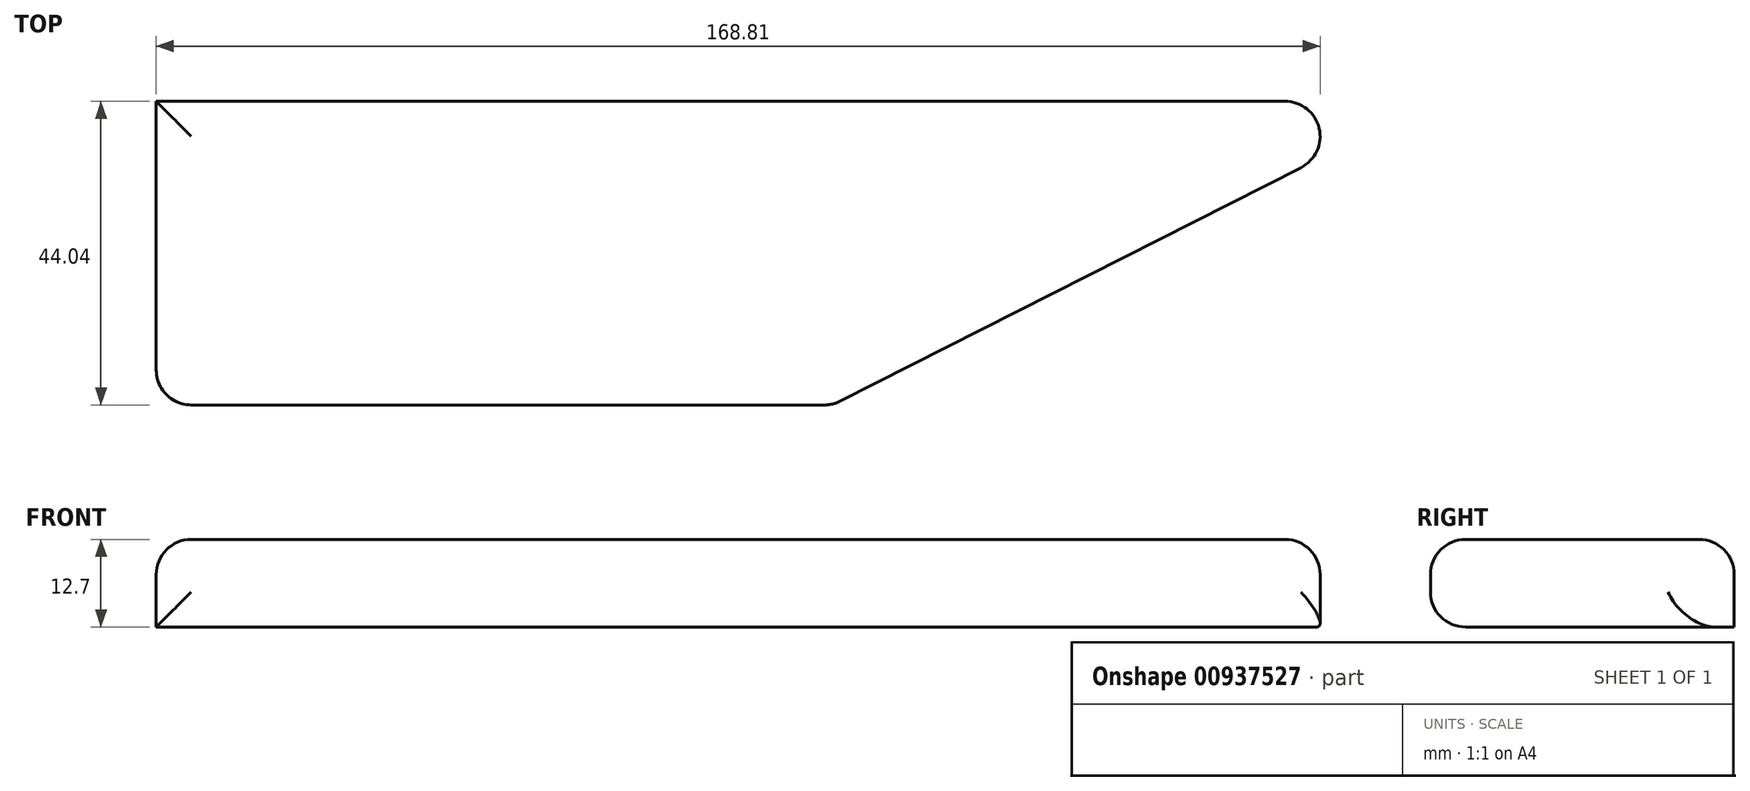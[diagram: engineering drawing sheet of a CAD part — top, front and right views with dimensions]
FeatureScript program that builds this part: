
annotation { "Feature Type Name" : "Feature", "Feature Type Description" : "" }
export const myFeature = defineFeature(function(context is Context, id is Id, definition is map)
    precondition{}
    {
        {
            var Q0;
            Q0=qCreatedBy(makeId("Top.planeOp"),FACE);
            var sketch = newSketch(context, id + "F0", { "sketchPlane" : qUnion([Q0])});
            skLineSegment(sketch, "E0", {"start": v(-44.9, 21.4) * mm, "end": v(-44.9, -24.6) * mm});
            skLineSegment(sketch, "E1", {"start": v(-44.9, -24.6) * mm, "end": v(53.22, -24.6) * mm});
            skLineSegment(sketch, "E2", {"start": v(53.22, -24.6) * mm, "end": v(140.08, 19.45) * mm});
            skLineSegment(sketch, "E3", {"start": v(140.08, 19.45) * mm, "end": v(-44.9, 19.45) * mm});
            skSolve(sketch);
        }
        {
            var Q0;
            {var subQ0=sQuery(id+"F0.wireOp",EDGE,"E1");Q0=makeQuery(id+"F0.imprint","IMPRINT",FACE,{"disambiguationData":[TD([[makeQuery(id+"F0.imprint","IMPRINT",EDGE,{"derivedFrom":subQ0}),1.0]])]});}
            extrude(context, id + "F1", {"entities" : qUnion([Q0]), "depth" : 12.7 * mm, "offsetDistance" : 25.4 * mm});
        }
        {
            var Q0;
            Q0=makeQuery(id+"F1.opExtrude","CAP_FACE",FACE,{"disambiguationData":[OSD([sQuery(id+"F0.wireOp",EDGE,"E0"),sQuery(id+"F0.wireOp",EDGE,"E1"),sQuery(id+"F0.wireOp",EDGE,"E2"),sQuery(id+"F0.wireOp",EDGE,"E3")])],"isStart":false});
            var Q1;
            Q1=makeQuery(id+"F1.opExtrude","SWEPT_FACE",FACE,{"disambiguationData":[OSD([sQuery(id+"F0.wireOp",EDGE,"E1")])]});
            var Q2;
            Q2=makeQuery(id+"F1.opExtrude","SWEPT_FACE",FACE,{"disambiguationData":[OSD([sQuery(id+"F0.wireOp",EDGE,"E2")])]});
            fillet(context, id + "F2", {"entities" : qUnion([Q0, Q1, Q2]), "radius" : 5.08 * mm, "tangentPropagation" : true, "allowEdgeOverflow" : false});
        }
        {
            var Q0;
            Q0=qCreatedBy(makeId("Right.planeOp"),FACE);
            var sketch = newSketch(context, id + "F3", { "sketchPlane" : qUnion([Q0])});
            skFitSpline(sketch, "E4", {"points": [v(-20.92, 13.58) * mm, v(0, 13.34) * mm, v(10.4, 9.18) * mm, v(19.2, 7.46) * mm, v(10.64, 0) * mm, v(-20.68, 0) * mm, v(-20.92, 13.58) * mm]});
            skSolve(sketch);
        }
        {
            var Q0;
            Q0=sQuery(id+"F3.wireOp",EDGE,"E4");
            extrude(context, id + "F4", {"bodyType" : ToolBodyType.SURFACE, "surfaceEntities" : qUnion([Q0]), "depth" : 152.4 * mm, "offsetDistance" : 25.4 * mm});
        }
    });
